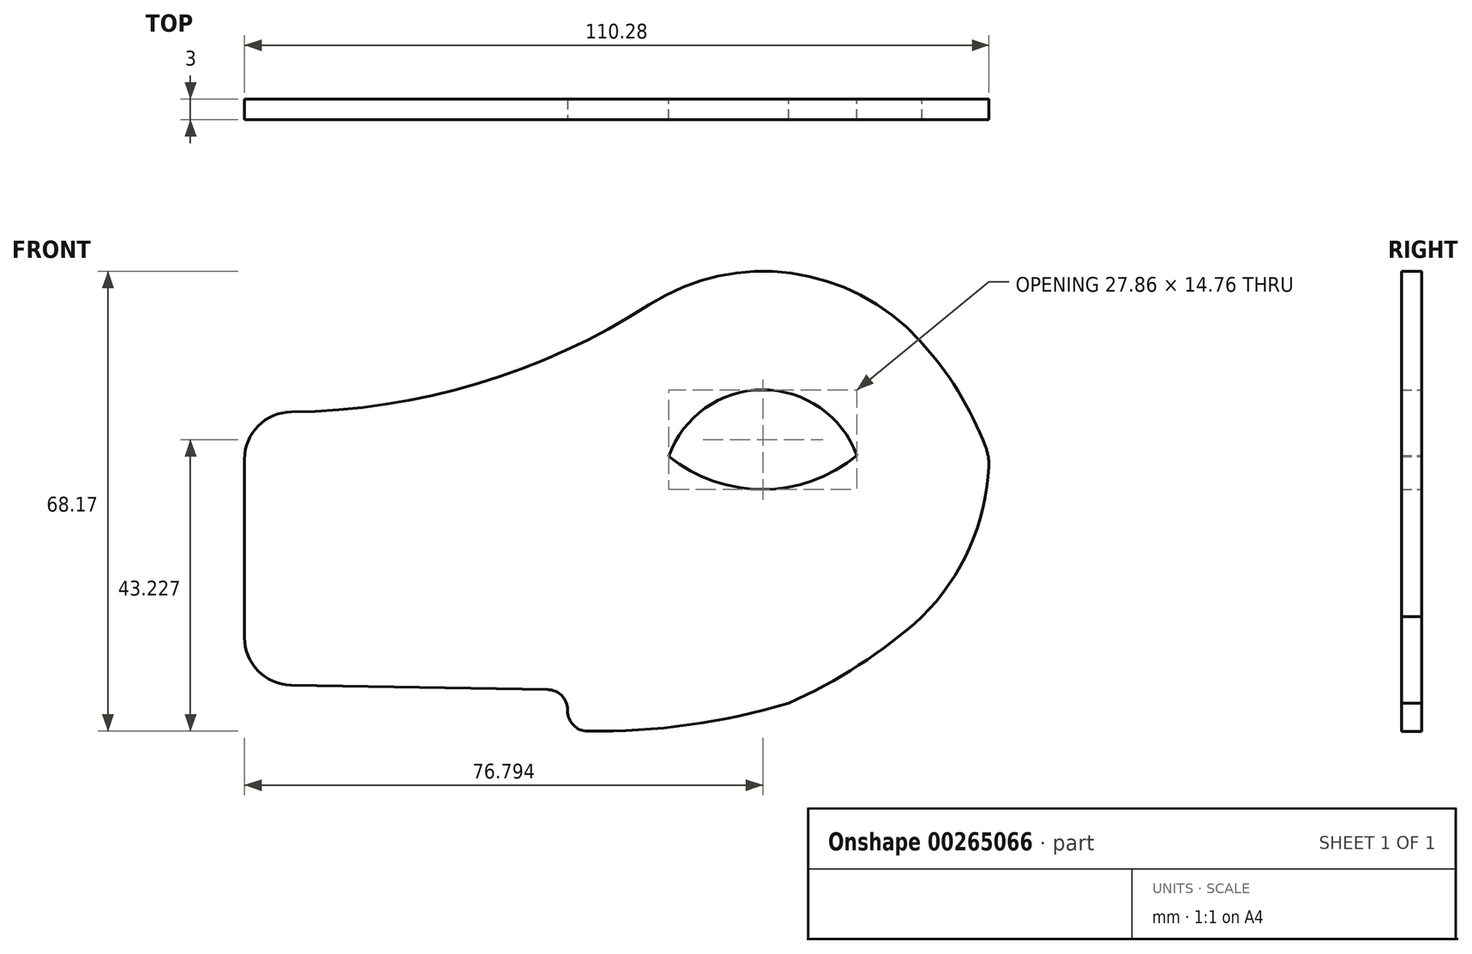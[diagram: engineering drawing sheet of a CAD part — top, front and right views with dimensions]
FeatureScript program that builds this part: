
annotation { "Feature Type Name" : "Feature", "Feature Type Description" : "" }
export const myFeature = defineFeature(function(context is Context, id is Id, definition is map)
    precondition{}
    {
        {
            var Q0;
            Q0=qCreatedBy(makeId("Front.planeOp"),FACE);
            var sketch = newSketch(context, id + "F0", { "sketchPlane" : qUnion([Q0])});
            skArc(sketch, "E0", {"start": v(-23.37, 71.6) * mm, "mid": v(-42.37, 87.06) * mm, "end": v(-61.37, 71.6) * mm});
            skPoint(sketch, "E1", {"position": v(-25.38, 77.03) * mm});
            skArc(sketch, "E2", {"start": v(-56.37, 71.6) * mm, "mid": v(-42.42, 66.69) * mm, "end": v(-28.5, 71.7) * mm});
            skArc(sketch, "E3", {"start": v(-28.5, 71.7) * mm, "mid": v(-42.48, 81.45) * mm, "end": v(-56.37, 71.6) * mm});
            skPoint(sketch, "E4", {"position": v(-42.37, 87.06) * mm});
            skPoint(sketch, "E5", {"position": v(-30.58, 56.7) * mm});
            skArc(sketch, "E6", {"start": v(-61.37, 71.6) * mm, "mid": v(-42.37, 52.6) * mm, "end": v(-23.37, 71.6) * mm});
            skPoint(sketch, "E7", {"position": v(-42.37, 52.6) * mm});
            skPoint(sketch, "E8", {"position": v(-61.37, 71.6) * mm});
            skPoint(sketch, "E9", {"position": v(-56.96, 80.44) * mm});
            skPoint(sketch, "E10", {"position": v(-68.92, 94.73) * mm});
            skPoint(sketch, "E11", {"position": v(-29.37, 71.03) * mm});
            skPoint(sketch, "E12", {"position": v(-85.15, 92.16) * mm});
            skPoint(sketch, "E13", {"position": v(-79.37, -8.64) * mm});
            skPoint(sketch, "E14.endSnap0", {"position": v(-42.4, 59.62) * mm});
            skLineSegment(sketch, "E15", {"start": v(-28.5, 71.7) * mm, "end": v(-23.37, 71.6) * mm});
            skLineSegment(sketch, "E16", {"start": v(-61.37, 71.6) * mm, "end": v(-56.37, 71.6) * mm});
            skLineSegment(sketch, "E17", {"start": v(-42.42, 66.69) * mm, "end": v(-42.42, 66.65) * mm});
            skPoint(sketch, "E18", {"position": v(-24.15, 66.23) * mm});
            skPoint(sketch, "E19", {"position": v(-59.84, 76.1) * mm});
            skPoint(sketch, "E20", {"position": v(-60.59, 66.2) * mm});
            skLineSegment(sketch, "E21.bottom", {"start": v(-26.7, 79.1) * mm, "end": v(-27.38, 79.1) * mm});
            skPoint(sketch, "E22", {"position": v(-108.66, 79.1) * mm});
            skLineSegment(sketch, "E23.top", {"start": v(-109.39, 67.1) * mm, "end": v(-109.78, 67.1) * mm});
            skLineSegment(sketch, "E24.left", {"start": v(-39.95, 71.09) * mm, "end": v(-39.95, 71.09) * mm});
            skLineSegment(sketch, "E24.right", {"start": v(-42.68, 71.09) * mm, "end": v(-42.68, 71.09) * mm});
            skLineSegment(sketch, "E25.top", {"start": v(-63.18, 66.2) * mm, "end": v(-68.59, 66.2) * mm});
            skPoint(sketch, "E26.orphan", {"position": v(-114.78, 67.1) * mm});
            skPoint(sketch, "E27.top.start.orphan", {"position": v(-109.78, 64.1) * mm});
            skPoint(sketch, "E14.end.orphan", {"position": v(-42.4, 81.45) * mm});
            skLineSegment(sketch, "E28.trimOffspring", {"start": v(-109.78, 54.6) * mm, "end": v(-109.78, 51.6) * mm});
            skPoint(sketch, "E29.top.end.orphan", {"position": v(-106.78, 10.37) * mm});
            skPoint(sketch, "E29.left.start.orphan", {"position": v(-109.78, 35.77) * mm});
            skPoint(sketch, "E24.bottom.start.orphan", {"position": v(-48.6, 10.37) * mm});
            skPoint(sketch, "E24.top.end.orphan", {"position": v(-51.33, 10.37) * mm});
            skPoint(sketch, "E30.start.orphan", {"position": v(-38.82, 35.77) * mm});
            skArc(sketch, "E31.0", {"start": v(-38.63, 35) * mm, "mid": v(-33.57, 45.03) * mm, "end": v(-28.58, 55.1) * mm});
            skLineSegment(sketch, "E31.2", {"start": v(-107.28, 66.2) * mm, "end": v(-107.28, 41.42) * mm});
            skLineSegment(sketch, "E32", {"start": v(-20.87, 71.6) * mm, "end": v(-23.37, 71.6) * mm});
            skLineSegment(sketch, "E33", {"start": v(-68.59, 66.2) * mm, "end": v(-107.28, 66.2) * mm});
            skArc(sketch, "E34.0", {"start": v(-63.87, 71.6) * mm, "mid": v(-42.37, 50.1) * mm, "end": v(-20.87, 71.6) * mm});
            skLineSegment(sketch, "E35", {"start": v(-61.37, 71.6) * mm, "end": v(-63.87, 71.6) * mm});
            skPoint(sketch, "E36", {"position": v(-80.6, -11.12) * mm});
            skPoint(sketch, "E37", {"position": v(-80.6, 66.2) * mm});
            skLineSegment(sketch, "E38.2", {"start": v(-119.23, 66.2) * mm, "end": v(-119.23, 47.82) * mm});
            skArc(sketch, "E39.0", {"start": v(-11.67, 74.02) * mm, "mid": v(-40.22, 98.93) * mm, "end": v(-71.9, 78.15) * mm});
            skLineSegment(sketch, "E40.0", {"start": v(-71.9, 78.15) * mm, "end": v(-107.28, 78.15) * mm});
            skArc(sketch, "E41.0", {"start": v(-18.85, 47.82) * mm, "mid": v(-11.5, 58.71) * mm, "end": v(-8.93, 71.6) * mm});
            skLineSegment(sketch, "E42", {"start": v(-119.23, 66.2) * mm, "end": v(-119.23, 78.15) * mm});
            skLineSegment(sketch, "E43", {"start": v(-107.28, 78.15) * mm, "end": v(-119.23, 78.15) * mm});
            skLineSegment(sketch, "E44", {"start": v(-8.93, 71.6) * mm, "end": v(-11.67, 71.6) * mm});
            skLineSegment(sketch, "E45", {"start": v(-11.67, 71.6) * mm, "end": v(-11.67, 74.02) * mm});
            skPoint(sketch, "E46.orphan", {"position": v(-73.06, 74.02) * mm});
            skPoint(sketch, "E47.end.orphan", {"position": v(-73.06, 71.6) * mm});
            skPoint(sketch, "E48.orphan", {"position": v(-119.23, 79.1) * mm});
            skPoint(sketch, "E49", {"position": v(-19.16, 88.73) * mm});
            skArc(sketch, "E50", {"start": v(-8.93, 71.6) * mm, "mid": v(-13.18, 80.68) * mm, "end": v(-19.16, 88.73) * mm});
            skPoint(sketch, "E51.orphan", {"position": v(-57.31, 4.66) * mm});
            skPoint(sketch, "E52", {"position": v(-42.45, 99) * mm});
            skLineSegment(sketch, "E53", {"start": v(-119.23, 47.82) * mm, "end": v(-119.23, 27.82) * mm});
            skArc(sketch, "E54.trimOffspring", {"start": v(-38.63, 35) * mm, "mid": v(-28.24, 40.62) * mm, "end": v(-18.85, 47.82) * mm});
            skPoint(sketch, "E55.start.orphan", {"position": v(-42.19, 33.52) * mm});
            skArc(sketch, "E56", {"start": v(-71.9, 30.95) * mm, "mid": v(-55.1, 31.57) * mm, "end": v(-38.63, 35) * mm});
            skArc(sketch, "E57", {"start": v(-119.23, 47.82) * mm, "mid": v(-96.43, 36.96) * mm, "end": v(-71.9, 30.95) * mm});
            skArc(sketch, "E58", {"start": v(-119.23, 37.82) * mm, "mid": v(-79.2, 28.8) * mm, "end": v(-38.63, 35) * mm});
            skPoint(sketch, "E59", {"position": v(-71.37, 28.8) * mm});
            skLineSegment(sketch, "E60", {"start": v(-71.37, 28.8) * mm, "end": v(-71.37, 36.96) * mm});
            skPoint(sketch, "E60.endSnap0", {"position": v(-96.43, 36.96) * mm});
            skLineSegment(sketch, "E61", {"start": v(-71.37, 36.96) * mm, "end": v(-119.23, 37.82) * mm});
            skSolve(sketch);
        }
        {
            var Q0;
            Q0=makeQuery(id+"F0.imprint","IMPRINT",FACE,{"disambiguationData":[TD([[makeQuery(id+"F0.imprint","IMPRINT",EDGE,{"derivedFrom":sQuery(id+"F0.wireOp",EDGE,"E3")}),-1.0]])]});
            var Q1;
            {var subQ2=sQuery(id+"F0.wireOp",EDGE,"E55");Q1=makeQuery(id+"F0.imprint","IMPRINT",FACE,{"disambiguationData":[TD([[makeQuery(id+"F0.imprint","IMPRINT",EDGE,{"derivedFrom":subQ2}),-1.0]])]});}
            var Q2;
            Q2=makeQuery(id+"F0.imprint","IMPRINT",FACE,{"disambiguationData":[TD([[makeQuery(id+"F0.imprint","IMPRINT",EDGE,{"derivedFrom":sQuery(id+"F0.wireOp",EDGE,"E6")}),1.0]])]});
            var Q3;
            {var subQ1=sQuery(id+"F0.wireOp",EDGE,"E55");Q3=makeQuery(id+"F0.imprint","IMPRINT",FACE,{"disambiguationData":[TD([[makeQuery(id+"F0.imprint","IMPRINT",EDGE,{"derivedFrom":subQ1}),1.0]])]});}
            var Q4;
            {var subQ0=sQuery(id+"F0.wireOp",EDGE,"E3");Q4=makeQuery(id+"F0.imprint","IMPRINT",FACE,{"disambiguationData":[TD([[makeQuery(id+"F0.imprint","IMPRINT",EDGE,{"derivedFrom":subQ0}),1.0]])]});}
            var Q5;
            Q5=makeQuery(id+"F0.imprint","IMPRINT",FACE,{"disambiguationData":[TD([[makeQuery(id+"F0.imprint","IMPRINT",EDGE,{"derivedFrom":sQuery(id+"F0.wireOp",EDGE,"E6")}),-1.0]])]});
            var Q6;
            {var subQ1=sQuery(id+"F0.wireOp",EDGE,"E25.top");Q6=makeQuery(id+"F0.imprint","IMPRINT",FACE,{"disambiguationData":[TD([[makeQuery(id+"F0.imprint","IMPRINT",EDGE,{"derivedFrom":subQ1}),-1.0]])]});}
            var Q7;
            Q7=makeQuery(id+"F0.imprint","IMPRINT",FACE,{"disambiguationData":[TD([[makeQuery(id+"F0.imprint","IMPRINT",EDGE,{"derivedFrom":sQuery(id+"F0.wireOp",EDGE,"E44")}),-1.0]])]});
            var Q8;
            {var subQ0=sQuery(id+"F0.wireOp",EDGE,"E53");Q8=makeQuery(id+"F0.imprint","IMPRINT",FACE,{"disambiguationData":[TD([[makeQuery(id+"F0.imprint","IMPRINT",EDGE,{"derivedFrom":subQ0}),1.0]])]});}
            var Q9;
            {var subQ2=sQuery(id+"F0.wireOp",EDGE,"E25.top");Q9=makeQuery(id+"F0.imprint","IMPRINT",FACE,{"disambiguationData":[TD([[makeQuery(id+"F0.imprint","IMPRINT",EDGE,{"derivedFrom":subQ2}),1.0]])]});}
            extrude(context, id + "F1", {"entities" : qUnion([Q0, Q1, Q2, Q3, Q4, Q5, Q6, Q7, Q8, Q9]), "depth" : 3 * mm, "offsetDistance" : 25 * mm});
        }
        {
            var Q0;
            {var subQ0=sQuery(id+"F0.wireOp",EDGE,"E3");Q0=makeQuery(id+"F0.imprint","IMPRINT",FACE,{"disambiguationData":[TD([[makeQuery(id+"F0.imprint","IMPRINT",EDGE,{"derivedFrom":subQ0}),1.0]])]});}
            extrude(context, id + "F2", {"entities" : qUnion([Q0]), "operationType" : NewBodyOperationType.REMOVE, "depth" : 25 * mm, "offsetDistance" : 25 * mm});
        }
        {
            var Q0;
            Q0=makeQuery(id+"F1.opExtrude","SWEPT_EDGE",EDGE,{"disambiguationData":[OSD([sQuery(id+"F0.wireOp",EDGE,"E38.2"),sQuery(id+"F0.wireOp",EDGE,"UHwYaH4J-JpYJ-icLg-BJ8S-10YJGJZzS52J")])]});
            var Q1;
            Q1=makeQuery(id+"F1.opExtrude","SWEPT_EDGE",EDGE,{"disambiguationData":[OSD([sQuery(id+"F0.wireOp",EDGE,"E41.0"),sQuery(id+"F0.wireOp",EDGE,"E44"),sQuery(id+"F0.wireOp",EDGE,"E50")])]});
            var Q2;
            Q2=makeQuery(id+"F1.opExtrude","SWEPT_EDGE",EDGE,{"disambiguationData":[OSD([sQuery(id+"F0.wireOp",EDGE,"E53"),sQuery(id+"F0.wireOp",EDGE,"9QbNPDRT-xxRn-6pHV-9aqg-9N1l9JF9NdzQ")])]});
            fillet(context, id + "F3", {"entities" : qUnion([Q0, Q1, Q2]), "radius" : 7 * mm, "tangentPropagation" : true, "defaultsChanged" : true, "vertexSettings" : [], "allowEdgeOverflow" : false});
        }
        {
            var Q0;
            Q0=makeQuery(id+"F1.opExtrude","SWEPT_EDGE",EDGE,{"disambiguationData":[OSD([sQuery(id+"F0.wireOp",EDGE,"E39.0"),sQuery(id+"F0.wireOp",EDGE,"E40.0")])]});
            fillet(context, id + "F4", {"entities" : qUnion([Q0]), "radius" : 100 * mm, "tangentPropagation" : true, "defaultsChanged" : false, "vertexSettings" : [], "allowEdgeOverflow" : false});
        }
        {
            var Q0;
            Q0=makeQuery(id+"F1.opExtrude","SWEPT_EDGE",EDGE,{"disambiguationData":[OSD([sQuery(id+"F0.wireOp",EDGE,"E42"),sQuery(id+"F0.wireOp",EDGE,"E43")])]});
            fillet(context, id + "F5", {"entities" : qUnion([Q0]), "radius" : 7 * mm, "tangentPropagation" : true, "defaultsChanged" : true, "vertexSettings" : [], "allowEdgeOverflow" : false});
        }
        {
            var Q0;
            Q0=makeQuery(id+"F1.opExtrude","SWEPT_EDGE",EDGE,{"disambiguationData":[OSD([sQuery(id+"F0.wireOp",EDGE,"E60"),sQuery(id+"F0.wireOp",EDGE,"E61")])]});
            var Q1;
            Q1=makeQuery(id+"F1.opExtrude","SWEPT_EDGE",EDGE,{"disambiguationData":[OSD([sQuery(id+"F0.wireOp",EDGE,"E56"),sQuery(id+"F0.wireOp",EDGE,"E60")])]});
            fillet(context, id + "F6", {"entities" : qUnion([Q0, Q1]), "tangentPropagation" : true, "radius" : 3 * mm, "defaultsChanged" : false, "vertexSettings" : [], "allowEdgeOverflow" : false});
        }
    });
